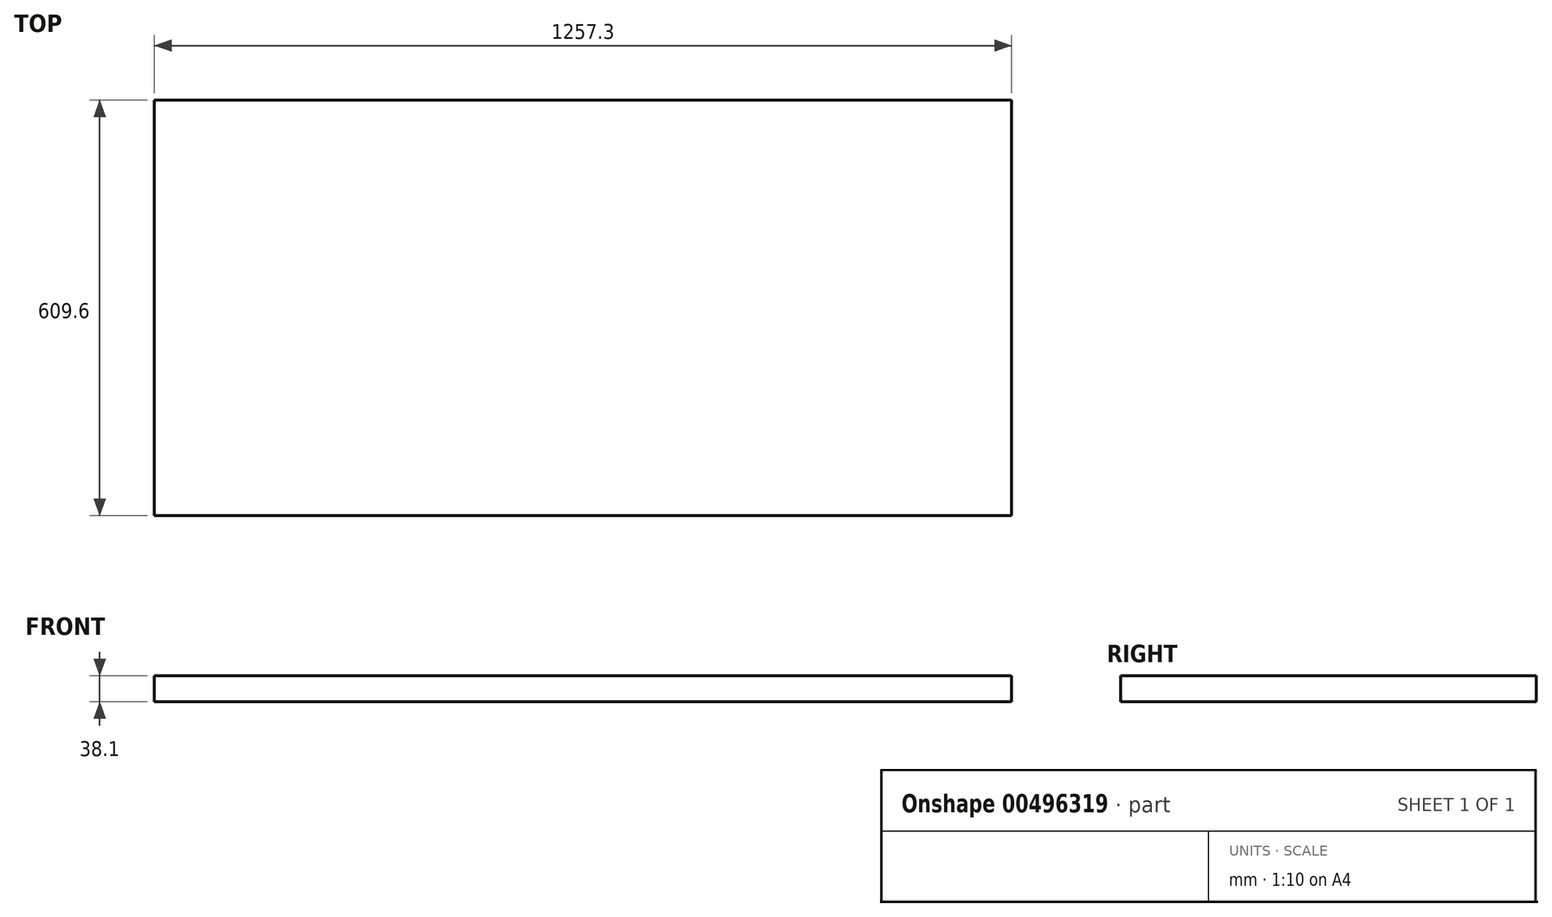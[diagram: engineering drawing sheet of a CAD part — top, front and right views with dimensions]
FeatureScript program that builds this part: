
annotation { "Feature Type Name" : "Feature", "Feature Type Description" : "" }
export const myFeature = defineFeature(function(context is Context, id is Id, definition is map)
    precondition{}
    {
        {
            var Q0;
            Q0=qCreatedBy(makeId("Top.planeOp"),FACE);
            var sketch = newSketch(context, id + "F0", { "sketchPlane" : qUnion([Q0])});
            skLineSegment(sketch, "E0.bottom", {"start": v(628.65, -304.8) * mm, "end": v(-628.65, -304.8) * mm});
            skLineSegment(sketch, "E0.top", {"start": v(628.65, 304.8) * mm, "end": v(-628.65, 304.8) * mm});
            skLineSegment(sketch, "E0.left", {"start": v(628.65, -304.8) * mm, "end": v(628.65, 304.8) * mm});
            skLineSegment(sketch, "E0.right", {"start": v(-628.65, -304.8) * mm, "end": v(-628.65, 304.8) * mm});
            skPoint(sketch, "E0.middle", {"position": v(0, 0) * mm});
            skSolve(sketch);
        }
        {
            var Q0;
            Q0 = qSketchRegion(id + "F0", true);
            extrude(context, id + "F1", {"entities" : qUnion([Q0]), "depth" : 38.1 * mm});
        }
    });
